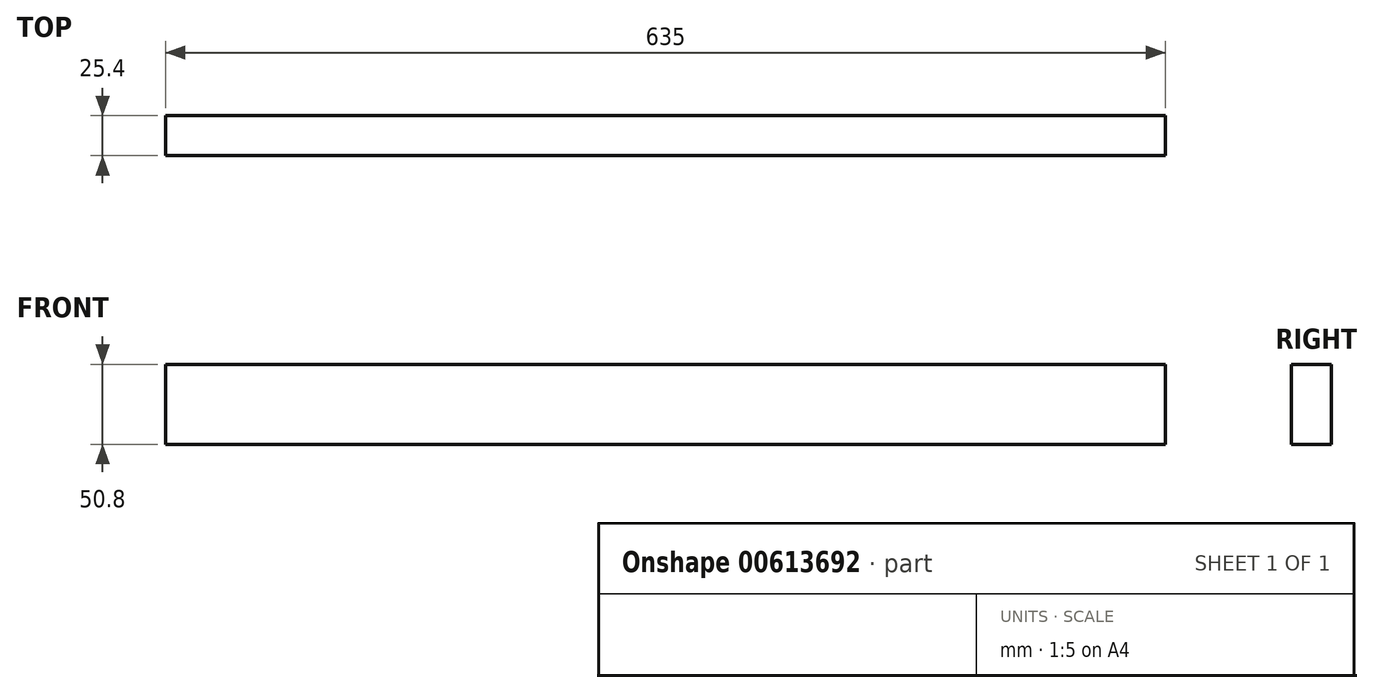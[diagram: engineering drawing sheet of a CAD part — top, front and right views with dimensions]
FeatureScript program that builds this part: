
annotation { "Feature Type Name" : "Feature", "Feature Type Description" : "" }
export const myFeature = defineFeature(function(context is Context, id is Id, definition is map)
    precondition{}
    {
        {
            var Q0;
            Q0=qCreatedBy(makeId("Front.planeOp"),FACE);
            var sketch = newSketch(context, id + "F0", { "sketchPlane" : qUnion([Q0])});
            skLineSegment(sketch, "E0.bottom", {"start": v(-322.86, 33.1) * mm, "end": v(312.14, 33.1) * mm});
            skLineSegment(sketch, "E0.top", {"start": v(-322.86, -17.7) * mm, "end": v(312.14, -17.7) * mm});
            skLineSegment(sketch, "E0.left", {"start": v(-322.86, 33.1) * mm, "end": v(-322.86, -17.7) * mm});
            skLineSegment(sketch, "E0.right", {"start": v(312.14, 33.1) * mm, "end": v(312.14, -17.7) * mm});
            skSolve(sketch);
        }
        {
            var Q0;
            Q0 = qSketchRegion(id + "F0", true);
            extrude(context, id + "F1", {"entities" : qUnion([Q0]), "depth" : 25.4 * mm, "offsetDistance" : 25.4 * mm});
        }
    });
